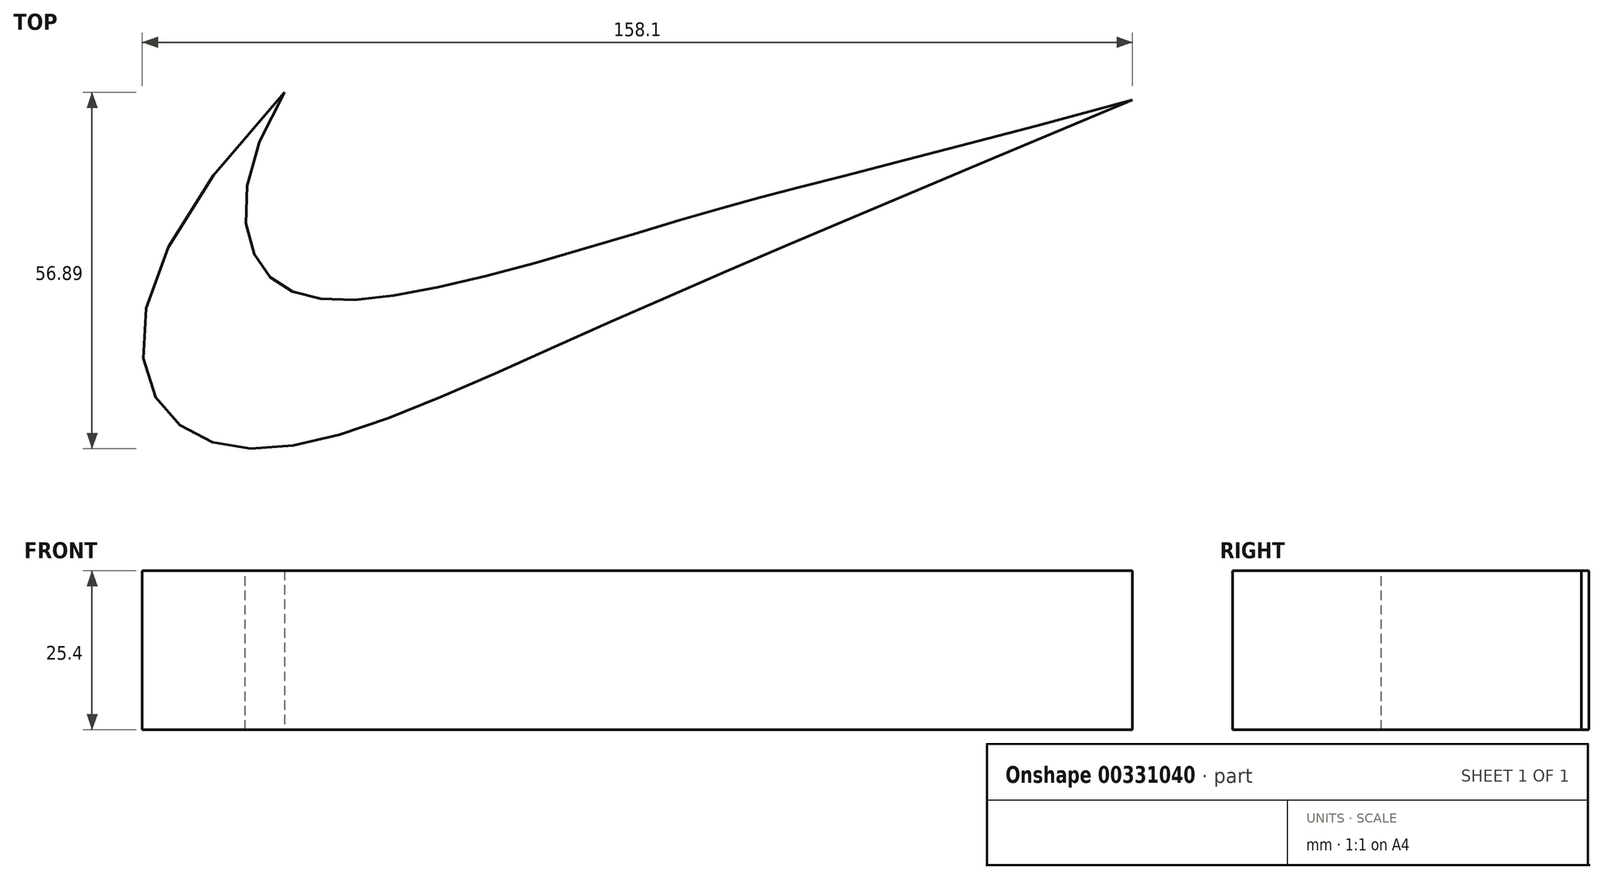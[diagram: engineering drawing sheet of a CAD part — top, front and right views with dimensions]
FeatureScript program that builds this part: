
annotation { "Feature Type Name" : "Feature", "Feature Type Description" : "" }
export const myFeature = defineFeature(function(context is Context, id is Id, definition is map)
    precondition{}
    {
        {
            var Q0;
            Q0=qCreatedBy(makeId("Top.planeOp"),FACE);
            var sketch = newSketch(context, id + "F0", { "sketchPlane" : qUnion([Q0])});
            skFitSpline(sketch, "E0", {"points": [v(-92.69, 8.04) * mm, v(-95.3, -21.13) * mm, v(-75.96, -24.5) * mm, v(-27.45, -11.77) * mm, v(42.7, 6.8) * mm], "startDerivative": vector(-118.76, -190.02) * mm, "endDerivative": vector(388.88, 105.21) * mm});
            skFitSpline(sketch, "E1", {"points": [v(-92.69, 8.04) * mm, v(-104.55, -47.7) * mm, v(-53.9, -34.5) * mm, v(42.7, 6.8) * mm], "startDerivative": vector(-314.09, -324.54) * mm, "endDerivative": vector(277.74, 115.48) * mm});
            skSolve(sketch);
        }
        {
            var Q0;
            Q0=makeQuery(id+"F0.imprint","IMPRINT",FACE,{"disambiguationData":[TD([[makeQuery(id+"F0.imprint","IMPRINT",EDGE,{"derivedFrom":sQuery(id+"F0.wireOp",EDGE,"E0")}),-1.0]])]});
            extrude(context, id + "F1", {"entities" : qUnion([Q0]), "depth" : 25.4 * mm, "offsetDistance" : 25.4 * mm});
        }
    });
